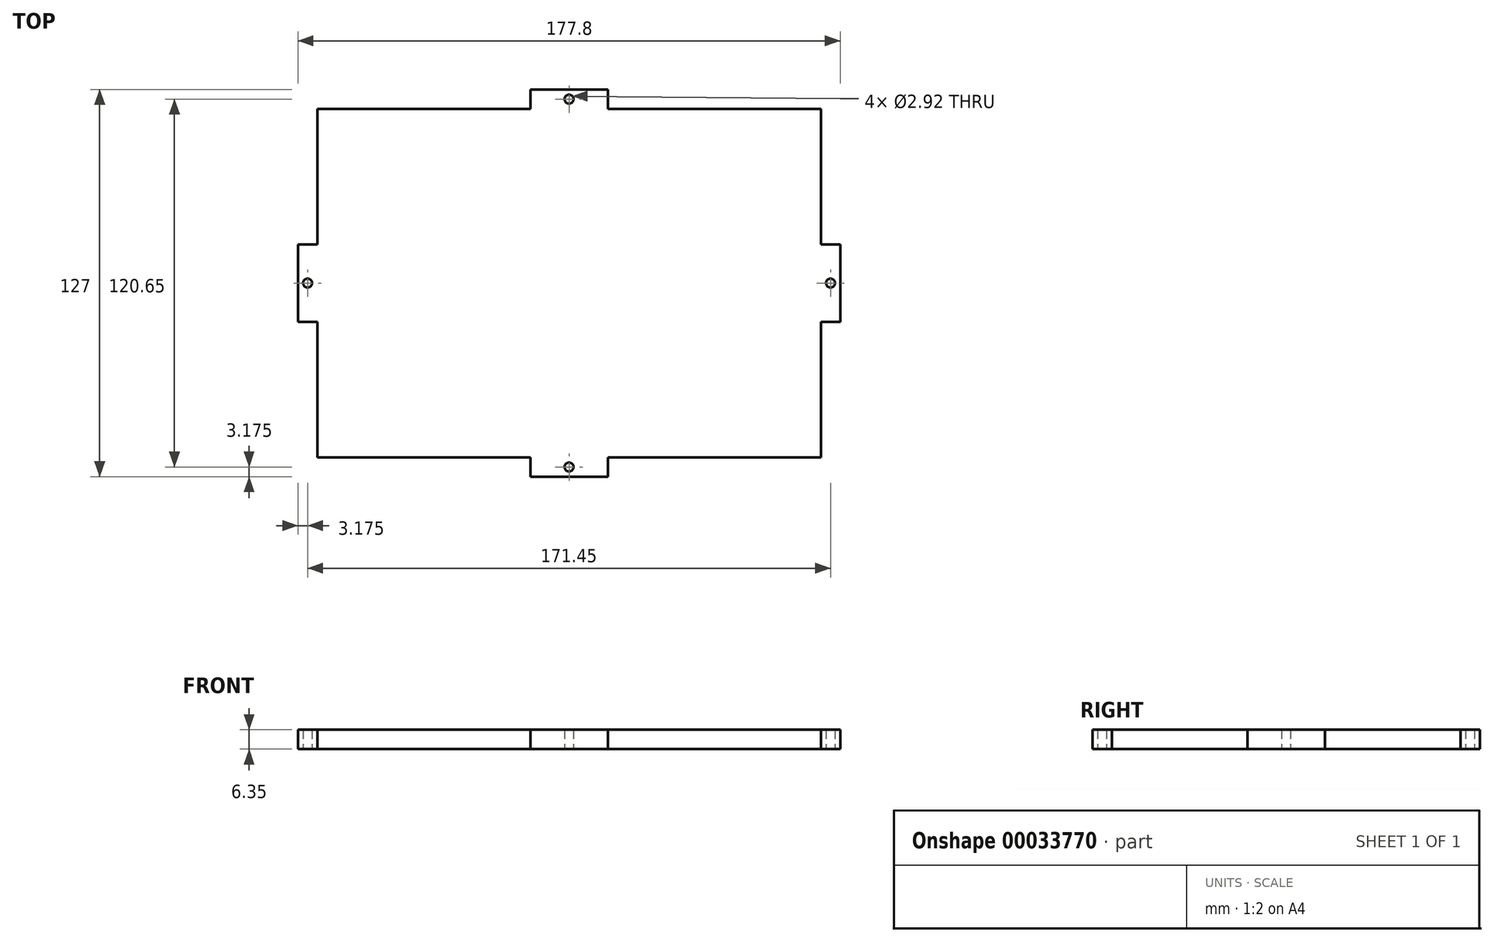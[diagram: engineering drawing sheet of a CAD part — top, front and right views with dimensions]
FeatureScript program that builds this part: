
annotation { "Feature Type Name" : "Feature", "Feature Type Description" : "" }
export const myFeature = defineFeature(function(context is Context, id is Id, definition is map)
    precondition{}
    {
        {
            var Q0;
            Q0=qCreatedBy(makeId("Top.planeOp"),FACE);
            var sketch = newSketch(context, id + "F0", { "sketchPlane" : qUnion([Q0])});
            skLineSegment(sketch, "E0.rect.bottom", {"start": v(12.7, -63.5) * mm, "end": v(-12.7, -63.5) * mm});
            skLineSegment(sketch, "E0.rect.left", {"start": v(88.9, -12.7) * mm, "end": v(88.9, 12.7) * mm});
            skLineSegment(sketch, "E0.rect.right", {"start": v(-88.9, -12.7) * mm, "end": v(-88.9, 12.7) * mm});
            skPoint(sketch, "E0.rect.middle", {"position": v(0, 0) * mm});
            skLineSegment(sketch, "E1", {"start": v(-88.9, 0) * mm, "end": v(-82.55, 0) * mm, "construction": true});
            skLineSegment(sketch, "E2", {"start": v(0, 63.5) * mm, "end": v(0, -63.5) * mm, "construction": true});
            skLineSegment(sketch, "E3.0", {"start": v(76.2, -63.5) * mm, "end": v(76.2, 63.5) * mm, "construction": true});
            skLineSegment(sketch, "E4.0", {"start": v(31.75, -63.5) * mm, "end": v(31.75, 63.5) * mm, "construction": true});
            skLineSegment(sketch, "E5.0", {"start": v(-6.35, -63.5) * mm, "end": v(-6.35, 63.5) * mm, "construction": true});
            skLineSegment(sketch, "E6.0", {"start": v(-44.45, -63.5) * mm, "end": v(-44.45, 63.5) * mm, "construction": true});
            skLineSegment(sketch, "E7.0", {"start": v(82.55, 57.15) * mm, "end": v(12.7, 57.15) * mm});
            skLineSegment(sketch, "E7.1", {"start": v(82.55, -57.15) * mm, "end": v(82.55, -12.7) * mm});
            skLineSegment(sketch, "E7.2", {"start": v(82.55, -57.15) * mm, "end": v(12.7, -57.15) * mm});
            skLineSegment(sketch, "E7.3", {"start": v(-82.55, -57.15) * mm, "end": v(-82.55, -12.7) * mm});
            skLineSegment(sketch, "E8.0", {"start": v(0, -63.5) * mm, "end": v(0, -57.15) * mm, "construction": true});
            skLineSegment(sketch, "E9.0", {"start": v(12.7, -63.5) * mm, "end": v(12.7, 63.5) * mm, "construction": true});
            skLineSegment(sketch, "E10.MirrorCS", {"start": v(-12.7, -63.5) * mm, "end": v(-12.7, 63.5) * mm, "construction": true});
            skLineSegment(sketch, "E11", {"start": v(-12.7, 63.5) * mm, "end": v(-12.7, 57.15) * mm});
            skLineSegment(sketch, "E12", {"start": v(12.7, 63.5) * mm, "end": v(12.7, 57.15) * mm});
            skLineSegment(sketch, "E13.trimOffspring", {"start": v(-12.7, 57.15) * mm, "end": v(-82.55, 57.15) * mm});
            skLineSegment(sketch, "E14.MirrorCS", {"start": v(-12.7, -63.5) * mm, "end": v(-12.7, -57.15) * mm});
            skLineSegment(sketch, "E15.MirrorCS", {"start": v(12.7, -63.5) * mm, "end": v(12.7, -57.15) * mm});
            skLineSegment(sketch, "E16.trimOffspring", {"start": v(-12.7, -57.15) * mm, "end": v(-82.55, -57.15) * mm});
            skLineSegment(sketch, "E17", {"start": v(-12.7, -57.15) * mm, "end": v(0, -57.15) * mm, "construction": true});
            skLineSegment(sketch, "E18", {"start": v(0, -57.15) * mm, "end": v(12.7, -57.15) * mm, "construction": true});
            skLineSegment(sketch, "E19", {"start": v(0, -57.15) * mm, "end": v(0, 63.5) * mm, "construction": true});
            skCircle(sketch, "E20", {"center": v(0, -60.32) * mm, "radius": 1.46 * mm});
            skCircle(sketch, "E21.MirrorC", {"center": v(0, 60.32) * mm, "radius": 1.46 * mm});
            skLineSegment(sketch, "E22.0", {"start": v(-88.9, -12.7) * mm, "end": v(88.9, -12.7) * mm, "construction": true});
            skLineSegment(sketch, "E23.MirrorCS", {"start": v(-88.9, 12.7) * mm, "end": v(88.9, 12.7) * mm, "construction": true});
            skLineSegment(sketch, "E24", {"start": v(-88.9, 12.7) * mm, "end": v(-82.55, 12.7) * mm});
            skLineSegment(sketch, "E25", {"start": v(-88.9, -12.7) * mm, "end": v(-82.55, -12.7) * mm});
            skLineSegment(sketch, "E26.trimOffspring", {"start": v(-82.55, 12.7) * mm, "end": v(-82.55, 57.15) * mm});
            skLineSegment(sketch, "E27", {"start": v(-82.55, 12.7) * mm, "end": v(-82.55, 0) * mm, "construction": true});
            skLineSegment(sketch, "E28", {"start": v(-82.55, 0) * mm, "end": v(-82.55, -12.7) * mm, "construction": true});
            skLineSegment(sketch, "E29", {"start": v(-82.55, 0) * mm, "end": v(88.9, 0) * mm, "construction": true});
            skCircle(sketch, "E30", {"center": v(-85.72, 0) * mm, "radius": 1.46 * mm});
            skLineSegment(sketch, "E31.MirrorCS", {"start": v(88.9, -12.7) * mm, "end": v(82.55, -12.7) * mm});
            skLineSegment(sketch, "E32.MirrorCS", {"start": v(88.9, 12.7) * mm, "end": v(82.55, 12.7) * mm});
            skCircle(sketch, "E33.MirrorC", {"center": v(85.72, 0) * mm, "radius": 1.46 * mm});
            skLineSegment(sketch, "E34.trimOffspring", {"start": v(82.55, 12.7) * mm, "end": v(82.55, 57.15) * mm});
            skPoint(sketch, "E35.orphan", {"position": v(-88.9, 63.5) * mm});
            skLineSegment(sketch, "E36.trimOffspring", {"start": v(12.7, 63.5) * mm, "end": v(-12.7, 63.5) * mm});
            skPoint(sketch, "E37.orphan", {"position": v(88.9, 63.5) * mm});
            skPoint(sketch, "E38.orphan", {"position": v(88.9, -63.5) * mm});
            skPoint(sketch, "E39.orphan", {"position": v(-88.9, -63.5) * mm});
            skSolve(sketch);
        }
        {
            var Q0;
            Q0=makeQuery(id+"F0.imprint","IMPRINT",FACE,{"disambiguationData":[TD([[makeQuery(id+"F0.imprint","IMPRINT",EDGE,{"derivedFrom":sQuery(id+"F0.wireOp",EDGE,"E0.rect.bottom")}),-1.0]])]});
            extrude(context, id + "F1", {"entities" : qUnion([Q0]), "depth" : 6.35 * mm});
        }
    });
